# Revit family: VFM2
name_source: partatom
category: Арматура трубопроводов
units: mm (PartAtom-declared; Revit-internal decimal feet)

## family parameters
Всегда вертикально = Да
На основе рабочей плоскости = Нет
Общий = Нет
При загрузке вырезать с полостями = Нет
Размер круглого соединителя = Использовать диаметр
Тип детали = Вставляется

## types (2) — shared parameters
ADSK_Версия Revit = 2019
ADSK_Версия семейства = 1.0
ADSK_Единица измерения = шт.
ADSK_Завод-изготовитель = ООО «Ридан-Трейд»
ADSK_Классификация нагрузок = Прочее
ADSK_Количество = 1
ADSK_Количество фаз = 1
ADSK_Коэффициент мощности = 1
ADSK_Материал = <По категории>
ADSK_Напряжение = 220 В
ADSK_Номинальная мощность = 18 Вт
ADSK_Полная мощность = 18 В·А
ADSK_Потеря давления жидкости = 0.0 Па
ADSK_Расход жидкости = 0.0000 м³/ч
LT = VFM-2R
URL = https://ridan.ru
d = 3 мм
e = 16 мм
u = 42 мм
v = 11 мм
w = 18 мм
x = 12 мм
ze = 18 мм
zf = 54 мм
zg = 38 мм
zh = 14 мм
zi = 9 мм
zj = 28 мм
zk = 12 мм

## per-type parameters (varying)
- DN80: ADSK_Диаметр условный=80 мм; ADSK_Код изделия=065B3501R; ADSK_Марка=VFM-2R DN80; ADSK_Масса=20; ADSK_Наименование=Клапан регулирующий седельный проходной VFM-2R PN16, Tmax=150C, DN80; ADSK_Пропускная способность=100.0000 м³/ч; a=71 мм; b=113 мм; c=93 мм; f=76 мм; g=273 мм; h=236 мм; i=140 мм; j=70 мм; k=86 мм; l=87 мм; m=21 мм; n=103 мм; o=107 мм; p=122 мм; q=187 мм; r=122 мм; s=150 мм; t=62 мм; y=141 мм; z=135 мм; za=200 мм; zb=148 мм; zc=61 мм; zl=310 мм; УГО_Длина=310 мм
- DN100: ADSK_Диаметр условный=100 мм; ADSK_Код изделия=065B3502R; ADSK_Марка=VFM-2R DN100; ADSK_Масса=26; ADSK_Наименование=Клапан регулирующий седельный проходной VFM-2R PN16, Tmax=150C, DN100; ADSK_Пропускная способность=160.0000 м³/ч; a=94 мм; b=134 мм; c=115 мм; f=100 мм; g=312 мм; h=263 мм; i=160 мм; j=100 мм; k=85 мм; l=98 мм; m=33 мм; n=114 мм; o=116 мм; p=131 мм; q=205 мм; r=132 мм; s=168 мм; t=70 мм; y=161 мм; z=155 мм; za=220 мм; zb=166 мм; zc=69 мм; zl=350 мм; УГО_Длина=350 мм
